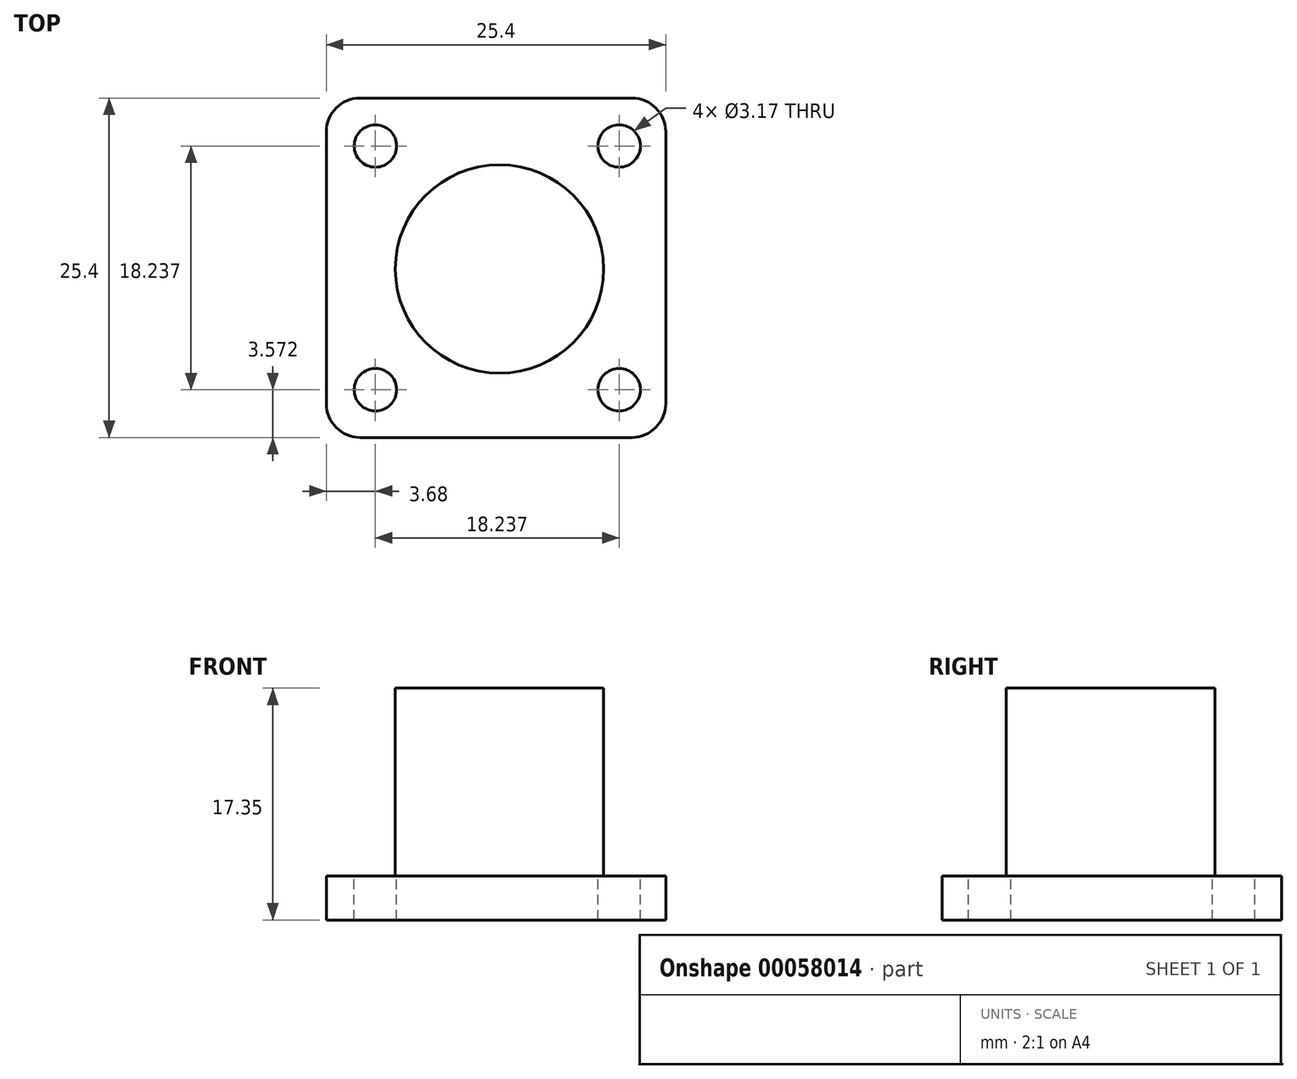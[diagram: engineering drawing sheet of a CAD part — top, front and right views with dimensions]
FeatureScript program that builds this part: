
annotation { "Feature Type Name" : "Feature", "Feature Type Description" : "" }
export const myFeature = defineFeature(function(context is Context, id is Id, definition is map)
    precondition{}
    {
        {
            var Q0;
            Q0=qCreatedBy(makeId("Top.planeOp"),FACE);
            var sketch = newSketch(context, id + "F0", { "sketchPlane" : qUnion([Q0])});
            skLineSegment(sketch, "E0.bottom", {"start": v(2.54, 0) * mm, "end": v(22.86, 0) * mm});
            skLineSegment(sketch, "E0.top", {"start": v(2.54, -25.4) * mm, "end": v(22.86, -25.4) * mm});
            skLineSegment(sketch, "E0.left", {"start": v(0, -2.54) * mm, "end": v(0, -22.86) * mm});
            skLineSegment(sketch, "E0.right", {"start": v(25.4, -2.54) * mm, "end": v(25.4, -22.86) * mm});
            skPoint(sketch, "E1.visualSharp", {"position": v(25.4, 0) * mm});
            skArc(sketch, "E1.filletArc", {"start": v(25.4, -2.54) * mm, "mid": v(24.66, -0.74) * mm, "end": v(22.86, 0) * mm});
            skPoint(sketch, "E2.visualSharp", {"position": v(25.4, -25.4) * mm});
            skArc(sketch, "E2.filletArc", {"start": v(22.86, -25.4) * mm, "mid": v(24.66, -24.66) * mm, "end": v(25.4, -22.86) * mm});
            skPoint(sketch, "E3.visualSharp", {"position": v(0, -25.4) * mm});
            skArc(sketch, "E3.filletArc", {"start": v(0, -22.86) * mm, "mid": v(0.74, -24.66) * mm, "end": v(2.54, -25.4) * mm});
            skPoint(sketch, "E4.visualSharp", {"position": v(0, 0) * mm});
            skArc(sketch, "E4.filletArc", {"start": v(2.54, 0) * mm, "mid": v(0.74, -0.74) * mm, "end": v(0, -2.54) * mm});
            skSolve(sketch);
        }
        {
            var Q0;
            Q0=makeQuery(id+"F0.imprint","IMPRINT",FACE,{"disambiguationData":[TD([[makeQuery(id+"F0.imprint","IMPRINT",EDGE,{"derivedFrom":sQuery(id+"F0.wireOp",EDGE,"E0.bottom")}),-1.0]])]});
            extrude(context, id + "F1", {"entities" : qUnion([Q0]), "depth" : 3.3 * mm});
        }
        {
            var Q0;
            Q0=makeQuery(id+"F1.opExtrude","CAP_FACE",FACE,{"disambiguationData":[OSD([sQuery(id+"F0.wireOp",EDGE,"E0.bottom"),sQuery(id+"F0.wireOp",EDGE,"E0.top"),sQuery(id+"F0.wireOp",EDGE,"E0.left"),sQuery(id+"F0.wireOp",EDGE,"E0.right"),sQuery(id+"F0.wireOp",EDGE,"E1.filletArc"),sQuery(id+"F0.wireOp",EDGE,"E2.filletArc"),sQuery(id+"F0.wireOp",EDGE,"E3.filletArc"),sQuery(id+"F0.wireOp",EDGE,"E4.filletArc")])],"isStart":false});
            var sketch = newSketch(context, id + "F2", { "sketchPlane" : qUnion([Q0])});
            skCircle(sketch, "E5", {"center": v(3.68, -21.83) * mm, "radius": 1.59 * mm});
            skCircle(sketch, "E6", {"center": v(21.92, -21.83) * mm, "radius": 1.59 * mm});
            skCircle(sketch, "E7", {"center": v(21.92, -3.6) * mm, "radius": 1.59 * mm});
            skCircle(sketch, "E8", {"center": v(3.68, -3.6) * mm, "radius": 1.59 * mm});
            skSolve(sketch);
        }
        {
            var Q0;
            Q0=qSketchRegion(id+"F2",true);
            extrude(context, id + "F3", {"entities" : qUnion([Q0]), "operationType" : NewBodyOperationType.REMOVE, "endBound" : BoundingType.THROUGH_ALL, "oppositeDirection" : true, "depth" : 25.4 * mm});
        }
        {
            var Q0;
            Q0=makeQuery(id+"F1.opExtrude","CAP_FACE",FACE,{"disambiguationData":[OSD([sQuery(id+"F0.wireOp",EDGE,"E0.bottom"),sQuery(id+"F0.wireOp",EDGE,"E0.top"),sQuery(id+"F0.wireOp",EDGE,"E0.left"),sQuery(id+"F0.wireOp",EDGE,"E0.right"),sQuery(id+"F0.wireOp",EDGE,"E1.filletArc"),sQuery(id+"F0.wireOp",EDGE,"E2.filletArc"),sQuery(id+"F0.wireOp",EDGE,"E3.filletArc"),sQuery(id+"F0.wireOp",EDGE,"E4.filletArc")])],"isStart":false});
            var sketch = newSketch(context, id + "F4", { "sketchPlane" : qUnion([Q0])});
            skCircle(sketch, "E9", {"center": v(12.96, -12.8) * mm, "radius": 7.8 * mm});
            skSolve(sketch);
        }
        {
            var Q0;
            Q0=makeQuery(id+"F4.imprint","IMPRINT",FACE,{"disambiguationData":[TD([[makeQuery(id+"F4.imprint","IMPRINT",EDGE,{"derivedFrom":sQuery(id+"F4.wireOp",EDGE,"E9")}),1.0]])]});
            extrude(context, id + "F5", {"entities" : qUnion([Q0]), "operationType" : NewBodyOperationType.ADD, "depth" : 14.05 * mm});
        }
    });
